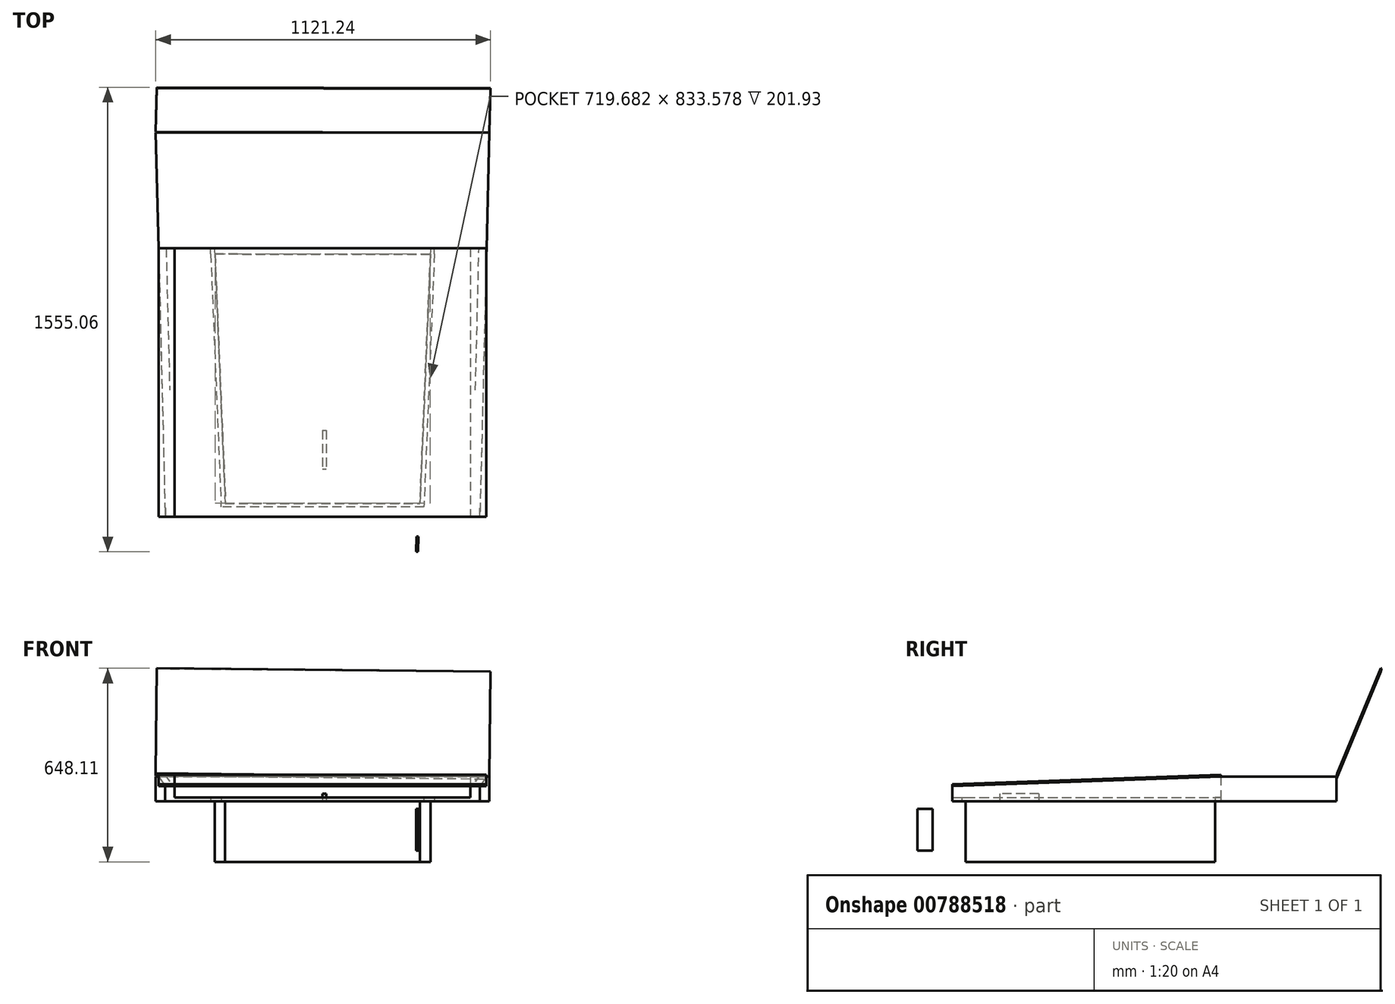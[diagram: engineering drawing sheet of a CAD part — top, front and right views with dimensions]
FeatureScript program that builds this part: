
annotation { "Feature Type Name" : "Feature", "Feature Type Description" : "" }
export const myFeature = defineFeature(function(context is Context, id is Id, definition is map)
    precondition{}
    {
        {
            var Q0;
            Q0=qCreatedBy(makeId("Top.planeOp"),FACE);
            var sketch = newSketch(context, id + "F0", { "sketchPlane" : qUnion([Q0])});
            skLineSegment(sketch, "E0", {"start": v(339.71, -803.8) * mm, "end": v(374.65, 31.75) * mm});
            skLineSegment(sketch, "E1", {"start": v(361.95, 50.8) * mm, "end": v(374.66, 50.8) * mm});
            skLineSegment(sketch, "E2", {"start": v(374.66, 50.8) * mm, "end": v(374.65, 31.75) * mm});
            skLineSegment(sketch, "E3", {"start": v(361.95, 50.8) * mm, "end": v(0, 50.8) * mm});
            skLineSegment(sketch, "E4", {"start": v(339.18, -815.98) * mm, "end": v(339.71, -803.8) * mm});
            skLineSegment(sketch, "E5.MirrorCS", {"start": v(-361.95, 50.8) * mm, "end": v(0, 50.8) * mm});
            skLineSegment(sketch, "E6.MirrorCS", {"start": v(-339.71, -803.8) * mm, "end": v(-374.65, 31.75) * mm});
            skLineSegment(sketch, "E7.MirrorCS", {"start": v(-374.66, 50.8) * mm, "end": v(-374.65, 31.75) * mm});
            skLineSegment(sketch, "E8.MirrorCS", {"start": v(-361.95, 50.8) * mm, "end": v(-374.66, 50.8) * mm});
            skLineSegment(sketch, "E9", {"start": v(-339.71, -803.8) * mm, "end": v(-339.18, -815.98) * mm});
            skLineSegment(sketch, "E10", {"start": v(0, 50.8) * mm, "end": v(495.3, 50.8) * mm});
            skLineSegment(sketch, "E11", {"start": v(495.3, 50.8) * mm, "end": v(495.3, 438.15) * mm});
            skLineSegment(sketch, "E12", {"start": v(0, -847.73) * mm, "end": v(495.3, -847.73) * mm});
            skLineSegment(sketch, "E13", {"start": v(495.3, -847.73) * mm, "end": v(495.3, 50.8) * mm});
            skLineSegment(sketch, "E14.MirrorCS", {"start": v(0, 50.8) * mm, "end": v(-495.3, 50.8) * mm});
            skLineSegment(sketch, "E15.MirrorCS", {"start": v(-495.3, 50.8) * mm, "end": v(-495.3, 438.15) * mm});
            skLineSegment(sketch, "E16.MirrorCS", {"start": v(-495.3, -847.73) * mm, "end": v(-495.3, 50.8) * mm});
            skLineSegment(sketch, "E17.MirrorCS", {"start": v(0, -847.73) * mm, "end": v(-495.3, -847.73) * mm});
            skLineSegment(sketch, "E18", {"start": v(-495.3, 438.15) * mm, "end": v(495.3, 438.15) * mm});
            skLineSegment(sketch, "E19", {"start": v(495.3, -847.73) * mm, "end": v(527.05, -847.73) * mm});
            skLineSegment(sketch, "E20", {"start": v(495.3, 438.15) * mm, "end": v(558.8, 438.15) * mm});
            skLineSegment(sketch, "E21.MirrorCS", {"start": v(-495.3, 438.15) * mm, "end": v(-558.8, 438.15) * mm});
            skLineSegment(sketch, "E22.MirrorCS", {"start": v(-495.3, -847.73) * mm, "end": v(-527.05, -847.73) * mm});
            skLineSegment(sketch, "E23", {"start": v(0, -558.8) * mm, "end": v(12.7, -558.8) * mm});
            skLineSegment(sketch, "E24", {"start": v(12.7, -558.8) * mm, "end": v(12.7, -690.19) * mm});
            skLineSegment(sketch, "E25", {"start": v(12.7, -690.19) * mm, "end": v(0, -690.19) * mm});
            skLineSegment(sketch, "E26", {"start": v(-495.3, 50.8) * mm, "end": v(-549.2, 49.47) * mm});
            skLineSegment(sketch, "E27", {"start": v(495.3, 50.8) * mm, "end": v(549.2, 49.47) * mm});
            skLineSegment(sketch, "E28", {"start": v(-558.8, 438.15) * mm, "end": v(-549.2, 49.47) * mm});
            skLineSegment(sketch, "E29", {"start": v(-549.2, 49.47) * mm, "end": v(-527.05, -847.73) * mm});
            skLineSegment(sketch, "E30", {"start": v(558.8, 438.15) * mm, "end": v(549.2, 49.47) * mm});
            skLineSegment(sketch, "E31", {"start": v(549.2, 49.47) * mm, "end": v(527.05, -847.73) * mm});
            skLineSegment(sketch, "E32", {"start": v(-339.71, -803.8) * mm, "end": v(339.71, -803.8) * mm});
            skLineSegment(sketch, "E33", {"start": v(-339.18, -815.98) * mm, "end": v(339.18, -815.98) * mm});
            skLineSegment(sketch, "E34", {"start": v(361.95, 50.8) * mm, "end": v(326.22, -803.8) * mm});
            skLineSegment(sketch, "E35", {"start": v(-361.95, 50.8) * mm, "end": v(-326.22, -803.8) * mm});
            skLineSegment(sketch, "E36", {"start": v(0, -558.8) * mm, "end": v(0, -690.19) * mm});
            skLineSegment(sketch, "E37", {"start": v(-374.65, 31.75) * mm, "end": v(-361.18, 32.31) * mm, "construction": true});
            skLineSegment(sketch, "E38", {"start": v(374.65, 31.75) * mm, "end": v(361.15, 31.75) * mm, "construction": true});
            skLineSegment(sketch, "E39", {"start": v(-361.18, 32.31) * mm, "end": v(361.15, 31.75) * mm});
            skSolve(sketch);
        }
        {
            var Q0;
            {var subQ1=sQuery(id+"F0.wireOp",EDGE,"E10");var subQ5=sQuery(id+"F0.wireOp",EDGE,"E14.MirrorCS");var subQ6=makeQuery(id+"F0.imprint","INTERSECT",VERTEX,{"derivedFrom":[subQ1,subQ5]});Q0=makeQuery(id+"F0.imprint","IMPRINT",FACE,{"disambiguationData":[TD([[makeQuery(id+"F0.imprint","IMPRINT",EDGE,{"disambiguationData":[TD([[subQ6,-1.0]])],"derivedFrom":subQ1}),-1.0]])]});}
            var Q1;
            {var subQ0=sQuery(id+"F0.wireOp",EDGE,"E7.MirrorCS");Q1=makeQuery(id+"F0.imprint","IMPRINT",FACE,{"disambiguationData":[TD([[makeQuery(id+"F0.imprint","IMPRINT",EDGE,{"derivedFrom":subQ0}),1.0]])]});}
            var Q2;
            {var subQ0=sQuery(id+"F0.wireOp",EDGE,"E6.MirrorCS");Q2=makeQuery(id+"F0.imprint","IMPRINT",FACE,{"disambiguationData":[TD([[makeQuery(id+"F0.imprint","IMPRINT",EDGE,{"derivedFrom":subQ0}),-1.0]])]});}
            var Q3;
            {var subQ0=sQuery(id+"F0.wireOp",EDGE,"E2");Q3=makeQuery(id+"F0.imprint","IMPRINT",FACE,{"disambiguationData":[TD([[makeQuery(id+"F0.imprint","IMPRINT",EDGE,{"derivedFrom":subQ0}),-1.0]])]});}
            var Q4;
            {var subQ0=sQuery(id+"F0.wireOp",EDGE,"E0");Q4=makeQuery(id+"F0.imprint","IMPRINT",FACE,{"disambiguationData":[TD([[makeQuery(id+"F0.imprint","IMPRINT",EDGE,{"derivedFrom":subQ0}),1.0]])]});}
            var Q5;
            {var subQ4=sQuery(id+"F0.wireOp",EDGE,"E4");Q5=makeQuery(id+"F0.imprint","IMPRINT",FACE,{"disambiguationData":[TD([[makeQuery(id+"F0.imprint","IMPRINT",EDGE,{"derivedFrom":subQ4}),1.0]])]});}
            extrude(context, id + "F1", {"entities" : qUnion([Q0, Q1, Q2, Q3, Q4, Q5]), "depth" : 1.27 * mm, "offsetDistance" : 25.4 * mm});
        }
        {
            var Q0;
            Q0=makeQuery(id+"F0.imprint","IMPRINT",FACE,{"disambiguationData":[TD([[makeQuery(id+"F0.imprint","IMPRINT",EDGE,{"derivedFrom":sQuery(id+"F0.wireOp",EDGE,"E23")}),1.0]])]});
            var Q1;
            Q1=makeQuery(id+"F0.imprint","IMPRINT",FACE,{"disambiguationData":[TD([[makeQuery(id+"F0.imprint","IMPRINT",EDGE,{"derivedFrom":sQuery(id+"F0.wireOp",EDGE,"E23")}),-1.0]])]});
            extrude(context, id + "F2", {"entities" : qUnion([Q0, Q1]), "operationType" : NewBodyOperationType.ADD, "oppositeDirection" : true, "depth" : 203.2 * mm, "offsetDistance" : 25.4 * mm});
        }
        {
            var Q0;
            Q0=makeQuery(id+"F2.opExtrude","CAP_FACE",FACE,{"disambiguationData":[OSD([sQuery(id+"F0.wireOp",EDGE,"m7xLVTAo-ODBZ-QKMM-9zlk-sLBRfuSS0PVQ"),sQuery(id+"F0.wireOp",EDGE,"E32"),sQuery(id+"F0.wireOp",EDGE,"E34"),sQuery(id+"F0.wireOp",EDGE,"E35")])],"isStart":true});
            shell(context, id + "F3", {"entities" : qUnion([Q0]), "thickness" : 1.27 * mm});
        }
        {
            var Q0;
            Q0=makeQuery(id+"F0.imprint","IMPRINT",FACE,{"disambiguationData":[TD([[makeQuery(id+"F0.imprint","IMPRINT",EDGE,{"derivedFrom":sQuery(id+"F0.wireOp",EDGE,"E0")}),-1.0]])]});
            extrude(context, id + "F4", {"entities" : qUnion([Q0]), "operationType" : NewBodyOperationType.ADD, "depth" : 12.7 * mm, "offsetDistance" : 25.4 * mm});
        }
        {
            var Q0;
            Q0=makeQuery(id+"F0.imprint","IMPRINT",FACE,{"disambiguationData":[TD([[makeQuery(id+"F0.imprint","IMPRINT",EDGE,{"derivedFrom":sQuery(id+"F0.wireOp",EDGE,"E13")}),-1.0]])]});
            var Q1;
            Q1=makeQuery(id+"F0.imprint","IMPRINT",FACE,{"disambiguationData":[TD([[makeQuery(id+"F0.imprint","IMPRINT",EDGE,{"derivedFrom":sQuery(id+"F0.wireOp",EDGE,"E16.MirrorCS")}),1.0]])]});
            extrude(context, id + "F5", {"entities" : qUnion([Q0, Q1]), "operationType" : NewBodyOperationType.ADD, "depth" : 50.8 * mm, "offsetDistance" : 25.4 * mm});
        }
        {
            var Q0;
            Q0=makeQuery(id+"F5.opExtrude","SWEPT_FACE",FACE,{"disambiguationData":[OSD([sQuery(id+"F0.wireOp",EDGE,"E31")])]});
            var sketch = newSketch(context, id + "F6", { "sketchPlane" : qUnion([Q0])});
            skLineSegment(sketch, "E40", {"start": v(63.01, 50.8) * mm, "end": v(63.01, 82.55) * mm});
            skLineSegment(sketch, "E41", {"start": v(63.01, 82.55) * mm, "end": v(-834.46, 50.8) * mm});
            skLineSegment(sketch, "E42", {"start": v(-834.46, 50.8) * mm, "end": v(63.01, 50.8) * mm});
            skSolve(sketch);
        }
        {
            var Q0;
            Q0=makeQuery(id+"F6.imprint","IMPRINT",FACE,{"disambiguationData":[TD([[makeQuery(id+"F6.imprint","IMPRINT",EDGE,{"derivedFrom":sQuery(id+"F6.wireOp",EDGE,"E40")}),1.0]])]});
            extrude(context, id + "F7", {"entities" : qUnion([Q0]), "oppositeDirection" : true, "depth" : 25.4 * mm, "offsetDistance" : 25.4 * mm});
        }
        {
            var Q0;
            Q0=makeQuery(id+"F5.opExtrude","SWEPT_FACE",FACE,{"disambiguationData":[OSD([sQuery(id+"F0.wireOp",EDGE,"E13")])]});
            var sketch = newSketch(context, id + "F8", { "sketchPlane" : qUnion([Q0])});
            skLineSegment(sketch, "E43", {"start": v(-50.8, 50.8) * mm, "end": v(-50.8, 82.55) * mm});
            skLineSegment(sketch, "E44", {"start": v(-50.8, 82.55) * mm, "end": v(847.73, 50.8) * mm});
            skLineSegment(sketch, "E45", {"start": v(847.73, 50.8) * mm, "end": v(-50.8, 50.8) * mm});
            skSolve(sketch);
        }
        {
            var Q0;
            Q0=makeQuery(id+"F8.imprint","IMPRINT",FACE,{"disambiguationData":[TD([[makeQuery(id+"F8.imprint","IMPRINT",EDGE,{"derivedFrom":sQuery(id+"F8.wireOp",EDGE,"E43")}),-1.0]])]});
            extrude(context, id + "F9", {"entities" : qUnion([Q0]), "oppositeDirection" : true, "depth" : 30.73 * mm, "offsetDistance" : 25.4 * mm});
        }
        {
            var Q0;
            Q0=makeQuery(id+"F0.imprint","IMPRINT",FACE,{"disambiguationData":[TD([[makeQuery(id+"F0.imprint","IMPRINT",EDGE,{"derivedFrom":sQuery(id+"F0.wireOp",EDGE,"E23")}),-1.0]])]});
            extrude(context, id + "F10", {"entities" : qUnion([Q0]), "depth" : 25.4 * mm, "offsetDistance" : 25.4 * mm});
        }
        {
            var Q0;
            Q0=makeQuery(id+"F9.opExtrude","SWEPT_BODY",BODY,{"disambiguationData":[OSD([sQuery(id+"F8.wireOp",EDGE,"E43"),sQuery(id+"F8.wireOp",EDGE,"E44"),sQuery(id+"F8.wireOp",EDGE,"E45")])]});
            var Q1;
            Q1=makeQuery(id+"F7.opExtrude","SWEPT_BODY",BODY,{"disambiguationData":[OSD([sQuery(id+"F6.wireOp",EDGE,"E40"),sQuery(id+"F6.wireOp",EDGE,"E41"),sQuery(id+"F6.wireOp",EDGE,"E42")])]});
            var Q2;
            Q2=makeQuery(id+"F10.opExtrude","SWEPT_FACE",FACE,{"disambiguationData":[OSD([sQuery(id+"F0.wireOp",EDGE,"E36")])]});
            mirror(context, id + "F11", {"operationType" : NewBodyOperationType.ADD, "entities" : qUnion([Q0, Q1]), "mirrorPlane" : qUnion([Q2])});
        }
        {
            var Q0;
            Q0=makeQuery(id+"F0.imprint","IMPRINT",FACE,{"disambiguationData":[TD([[makeQuery(id+"F0.imprint","IMPRINT",EDGE,{"derivedFrom":sQuery(id+"F0.wireOp",EDGE,"E11")}),-1.0]])]});
            var Q1;
            Q1=makeQuery(id+"F0.imprint","IMPRINT",FACE,{"disambiguationData":[TD([[makeQuery(id+"F0.imprint","IMPRINT",EDGE,{"derivedFrom":sQuery(id+"F0.wireOp",EDGE,"E15.MirrorCS")}),1.0]])]});
            extrude(context, id + "F12", {"entities" : qUnion([Q0, Q1]), "operationType" : NewBodyOperationType.ADD, "depth" : 82.55 * mm, "offsetDistance" : 25.4 * mm});
        }
        {
            var Q0;
            {var subQ0=sQuery(id+"F0.wireOp",EDGE,"E11");Q0=makeQuery(id+"F0.imprint","IMPRINT",FACE,{"disambiguationData":[TD([[makeQuery(id+"F0.imprint","IMPRINT",EDGE,{"derivedFrom":subQ0}),1.0]])]});}
            extrude(context, id + "F13", {"entities" : qUnion([Q0]), "operationType" : NewBodyOperationType.ADD, "depth" : 82.55 * mm, "offsetDistance" : 25.4 * mm});
        }
        {
            var Q0;
            Q0=makeQuery(id+"F12.boolean.opBoolean","MERGE",FACE,{"derivedFrom":[makeQuery(id+"F11.boolean.opBoolean","MERGE",FACE,{"derivedFrom":[makeQuery(id+"F5.opExtrude","SWEPT_FACE",FACE,{"disambiguationData":[OSD([sQuery(id+"F0.wireOp",EDGE,"E16.MirrorCS")])]}),makeQuery(id+"F11.opPattern","COPY",FACE,{"derivedFrom":makeQuery(id+"F9.opExtrude","CAP_FACE",FACE,{"disambiguationData":[OSD([sQuery(id+"F8.wireOp",EDGE,"E43"),sQuery(id+"F8.wireOp",EDGE,"E44"),sQuery(id+"F8.wireOp",EDGE,"E45")])],"isStart":true}),"instanceName":"1"})]}),makeQuery(id+"F12.opExtrude","SWEPT_FACE",FACE,{"disambiguationData":[OSD([sQuery(id+"F0.wireOp",EDGE,"E15.MirrorCS")])]})]});
            var sketch = newSketch(context, id + "F14", { "sketchPlane" : qUnion([Q0])});
            skLineSegment(sketch, "E46", {"start": v(-847.73, 50.8) * mm, "end": v(-847.95, 57.15) * mm});
            skLineSegment(sketch, "E47", {"start": v(-847.95, 57.15) * mm, "end": v(50.8, 88.9) * mm});
            skLineSegment(sketch, "E48", {"start": v(50.8, 88.9) * mm, "end": v(50.8, 82.55) * mm});
            skLineSegment(sketch, "E49", {"start": v(50.8, 82.55) * mm, "end": v(-847.73, 50.8) * mm});
            skSolve(sketch);
        }
        {
            var Q0;
            Q0=makeQuery(id+"F14.imprint","IMPRINT",FACE,{"disambiguationData":[TD([[makeQuery(id+"F14.imprint","IMPRINT",EDGE,{"derivedFrom":sQuery(id+"F14.wireOp",EDGE,"E46")}),-1.0]])]});
            extrude(context, id + "F15", {"entities" : qUnion([Q0]), "depth" : 1043.94 * mm, "offsetDistance" : 25.4 * mm});
        }
        {
            var Q0;
            Q0=makeQuery(id+"F15.opExtrude","CAP_FACE",FACE,{"disambiguationData":[OSD([sQuery(id+"F14.wireOp",EDGE,"E46"),sQuery(id+"F14.wireOp",EDGE,"E47"),sQuery(id+"F14.wireOp",EDGE,"E48"),sQuery(id+"F14.wireOp",EDGE,"E49")])],"isStart":true});
            extrude(context, id + "F16", {"entities" : qUnion([Q0]), "depth" : 53.34 * mm, "offsetDistance" : 25.4 * mm});
        }
        {
            var Q0;
            Q0=makeQuery(id+"F2.opExtrude","SWEPT_FACE",FACE,{"disambiguationData":[OSD([sQuery(id+"F0.wireOp",EDGE,"E34")])]});
            var sketch = newSketch(context, id + "F17", { "sketchPlane" : qUnion([Q0])});
            skLineSegment(sketch, "E50", {"start": v(-789.48, 0) * mm, "end": v(-789.48, -25.4) * mm});
            skLineSegment(sketch, "E51", {"start": v(-789.48, -25.4) * mm, "end": v(-789.48, -25.4) * mm});
            skLineSegment(sketch, "E52", {"start": v(-789.48, -25.4) * mm, "end": v(-789.48, 0) * mm});
            skLineSegment(sketch, "E53", {"start": v(-789.48, -25.4) * mm, "end": v(-900.6, -25.4) * mm});
            skLineSegment(sketch, "E54", {"start": v(-900.6, -25.4) * mm, "end": v(-951.4, -25.4) * mm});
            skLineSegment(sketch, "E55", {"start": v(-951.4, -25.4) * mm, "end": v(-951.4, -165.1) * mm});
            skLineSegment(sketch, "E56", {"start": v(-951.4, -165.1) * mm, "end": v(-900.6, -165.1) * mm});
            skLineSegment(sketch, "E57", {"start": v(-900.6, -165.1) * mm, "end": v(-900.6, -25.4) * mm});
            skLineSegment(sketch, "E58", {"start": v(-951.4, -25.4) * mm, "end": v(-1002.2, -25.4) * mm});
            skLineSegment(sketch, "E59", {"start": v(-1002.2, -25.4) * mm, "end": v(-1002.2, -165.1) * mm});
            skLineSegment(sketch, "E60", {"start": v(-1002.2, -165.1) * mm, "end": v(-1053, -165.1) * mm});
            skLineSegment(sketch, "E61", {"start": v(-1053, -165.1) * mm, "end": v(-1053, -25.4) * mm});
            skLineSegment(sketch, "E62", {"start": v(-1053, -25.4) * mm, "end": v(-1208.58, -25.4) * mm});
            skLineSegment(sketch, "E63", {"start": v(-1208.58, -25.4) * mm, "end": v(-1208.58, -165.1) * mm});
            skLineSegment(sketch, "E64", {"start": v(-1208.58, -165.1) * mm, "end": v(-1259.38, -165.1) * mm});
            skLineSegment(sketch, "E65", {"start": v(-1259.38, -165.1) * mm, "end": v(-1259.38, -25.4) * mm});
            skLineSegment(sketch, "E66", {"start": v(-1259.38, -25.4) * mm, "end": v(-1307, -25.4) * mm});
            skLineSegment(sketch, "E67", {"start": v(-1307, -25.4) * mm, "end": v(-1307, -165.1) * mm});
            skLineSegment(sketch, "E68", {"start": v(-1307, -165.1) * mm, "end": v(-1357.8, -165.1) * mm});
            skLineSegment(sketch, "E69", {"start": v(-1357.8, -165.1) * mm, "end": v(-1357.8, -25.4) * mm});
            skSolve(sketch);
        }
        {
            var Q0;
            Q0=makeQuery(id+"F17.imprint","IMPRINT",FACE,{"disambiguationData":[TD([[makeQuery(id+"F17.imprint","IMPRINT",EDGE,{"derivedFrom":sQuery(id+"F17.wireOp",EDGE,"E54")}),1.0]])]});
            var Q1;
            {var subQ0=sQuery(id+"F17.wireOp",EDGE,"E59");Q1=makeQuery(id+"F17.imprint","IMPRINT",FACE,{"disambiguationData":[TD([[makeQuery(id+"F17.imprint","IMPRINT",EDGE,{"derivedFrom":subQ0}),-1.0]])]});}
            var Q2;
            {var subQ0=sQuery(id+"F17.wireOp",EDGE,"E63");Q2=makeQuery(id+"F17.imprint","IMPRINT",FACE,{"disambiguationData":[TD([[makeQuery(id+"F17.imprint","IMPRINT",EDGE,{"derivedFrom":subQ0}),-1.0]])]});}
            var Q3;
            {var subQ0=sQuery(id+"F17.wireOp",EDGE,"E67");Q3=makeQuery(id+"F17.imprint","IMPRINT",FACE,{"disambiguationData":[TD([[makeQuery(id+"F17.imprint","IMPRINT",EDGE,{"derivedFrom":subQ0}),-1.0]])]});}
            extrude(context, id + "F18", {"entities" : qUnion([Q0, Q1, Q2, Q3]), "operationType" : NewBodyOperationType.ADD, "oppositeDirection" : true, "depth" : 6.35 * mm, "offsetDistance" : 25.4 * mm});
        }
        {
            var Q0;
            Q0=makeQuery(id+"F12.boolean.opBoolean","MERGE",FACE,{"derivedFrom":[makeQuery(id+"F11.boolean.opBoolean","MERGE",FACE,{"derivedFrom":[makeQuery(id+"F5.opExtrude","SWEPT_FACE",FACE,{"disambiguationData":[OSD([sQuery(id+"F0.wireOp",EDGE,"E31")])]}),makeQuery(id+"F7.opExtrude","CAP_FACE",FACE,{"disambiguationData":[OSD([sQuery(id+"F6.wireOp",EDGE,"E40"),sQuery(id+"F6.wireOp",EDGE,"E41"),sQuery(id+"F6.wireOp",EDGE,"E42")])],"isStart":true})]}),makeQuery(id+"F12.opExtrude","SWEPT_FACE",FACE,{"disambiguationData":[OSD([sQuery(id+"F0.wireOp",EDGE,"E30")])]})]});
            var sketch = newSketch(context, id + "F19", { "sketchPlane" : qUnion([Q0])});
            skLineSegment(sketch, "E70", {"start": v(451.8, 82.55) * mm, "end": v(597.87, 434.44) * mm});
            skLineSegment(sketch, "E71", {"start": v(597.87, 434.44) * mm, "end": v(600.8, 433.22) * mm});
            skLineSegment(sketch, "E72", {"start": v(600.8, 433.22) * mm, "end": v(451.8, 74.27) * mm});
            skSolve(sketch);
        }
        {
            var Q0;
            {var subQ0=sQuery(id+"F19.wireOp",EDGE,"E70");Q0=makeQuery(id+"F19.imprint","IMPRINT",FACE,{"disambiguationData":[TD([[makeQuery(id+"F19.imprint","IMPRINT",EDGE,{"derivedFrom":subQ0}),-1.0]])]});}
            extrude(context, id + "F20", {"entities" : qUnion([Q0]), "oppositeDirection" : true, "depth" : 1117.6 * mm, "offsetDistance" : 25.4 * mm});
        }
        {
            var Q0;
            Q0=makeQuery(id+"F20.opExtrude","SWEPT_BODY",BODY,{"disambiguationData":[OSD([sQuery(id+"F0.wireOp",EDGE,"E20"),sQuery(id+"F0.wireOp",EDGE,"E30"),sQuery(id+"F19.wireOp",EDGE,"E70"),sQuery(id+"F19.wireOp",EDGE,"E71"),sQuery(id+"F19.wireOp",EDGE,"E72")])]});
            var Q1;
            Q1=makeQuery(id+"F20.opExtrude","CAP_EDGE",EDGE,{"disambiguationData":[OSD([sQuery(id+"F19.wireOp",EDGE,"E70")])],"isStart":true});
            transform(context, id + "F21", {"entities" : qUnion([Q0]), "transformType" : TransformType.ROTATION, "transformAxis" : qUnion([Q1]), "angle" : 1.4 * degree, "makeCopy" : false});
        }
    });
